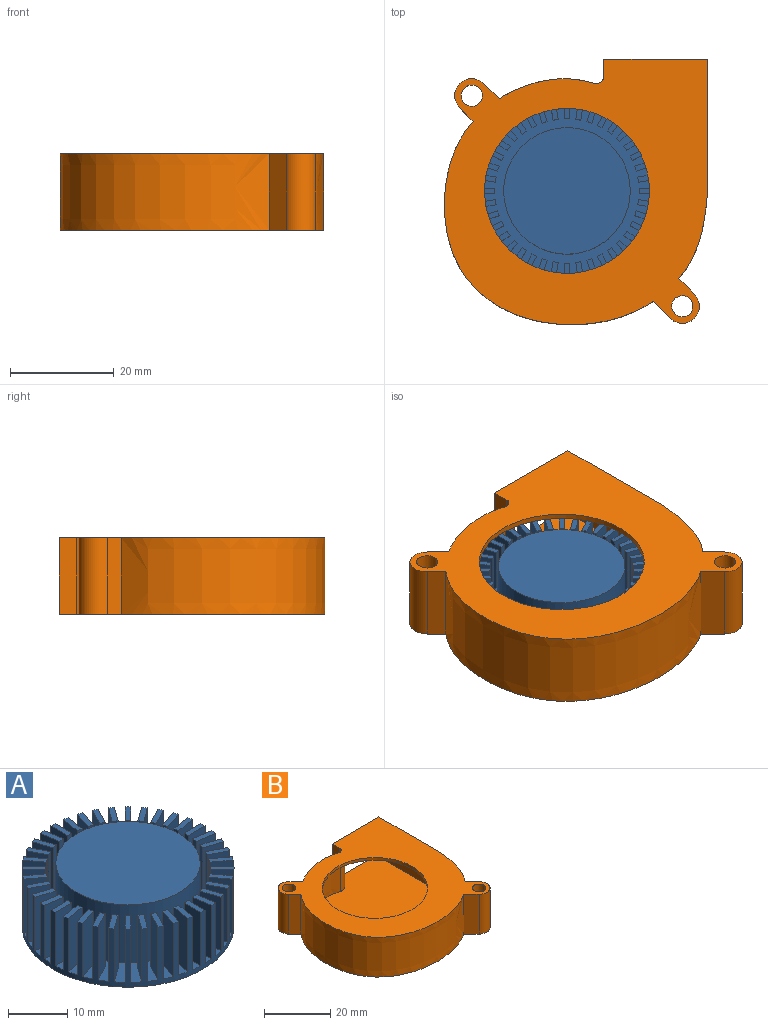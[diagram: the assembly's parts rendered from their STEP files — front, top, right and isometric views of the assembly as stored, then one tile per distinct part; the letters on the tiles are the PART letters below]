
ASSEMBLY  parts=2 mates=1
PART A: 165 faces, bbox 35.8x35.8x13 mm
  f0: plane 11x3.56mm, normal (-0.45,0.89,0), area 44mm2, adj f1,f3,f4,f6
  f1: cylinder r=17.91mm len=35.81mm, axis (0,0,-1), area 552.6mm2, adj f0,f2,f4,f5,f6,f7,f8,f10
  f2: plane 11x3.56mm, normal (0.45,-0.89,0), area 44mm2, adj f1,f3,f4,f6
  f3: plane 11x0.89mm, normal (0.89,0.45,0), area 11mm2, adj f0,f2,f4,f6
  f4: plane 4.02x2.71mm, normal (0,0,1), area 4mm2, adj f0,f1,f2,f3
  f5: plane 35.81x35.81mm, normal (0,0,-1), area 1007.4mm2, adj f1
  f6: plane 35.8x35.8mm, normal (0,0,1), area 379.6mm2, adj f0,f1,f2,f3,f7,f8,f9,f11
  f7: plane 11x3.8mm, normal (0.95,-0.31,0), area 44mm2, adj f1,f6,f9,f10
  f8: plane 11x3.8mm, normal (-0.95,0.31,0), area 44mm2, adj f1,f6,f9,f10
  f9: plane 11x0.95mm, normal (-0.31,-0.95,0), area 11mm2, adj f6,f7,f8,f10
  f10: plane 4.11x2.19mm, normal (0,0,1), area 4mm2, adj f1,f7,f8,f9
  f11: plane 11x3.95mm, normal (0.99,-0.16,0), area 44mm2, adj f1,f6,f13,f14
  f12: plane 11x3.95mm, normal (-0.99,0.16,0), area 44mm2, adj f1,f6,f13,f14
  f13: plane 11x0.99mm, normal (-0.16,-0.99,0), area 11mm2, adj f6,f11,f12,f14
  f14: plane 4.11x1.61mm, normal (0,0,1), area 4mm2, adj f1,f11,f12,f13
  f15: plane 11x3.8mm, normal (0.31,-0.95,0), area 44mm2, adj f1,f6,f17,f18
  f16: plane 11x3.8mm, normal (-0.31,0.95,0), area 44mm2, adj f1,f6,f17,f18
  f17: plane 11x0.95mm, normal (-0.95,-0.31,0), area 11mm2, adj f6,f15,f16,f18
  f18: plane 4.11x2.19mm, normal (0,0,1), area 4mm2, adj f1,f15,f16,f17
  f19: plane 11x3.56mm, normal (0.89,-0.45,0), area 44mm2, adj f1,f6,f21,f22
  f20: plane 11x3.56mm, normal (-0.89,0.45,0), area 44mm2, adj f1,f6,f21,f22
  f21: plane 11x0.89mm, normal (-0.45,-0.89,0), area 11mm2, adj f6,f19,f20,f22
  f22: plane 4.02x2.71mm, normal (0,0,1), area 4mm2, adj f1,f19,f20,f21
  f23: plane 11x3.95mm, normal (-0.99,-0.16,0), area 44mm2, adj f1,f6,f25,f26
  f24: plane 11x3.95mm, normal (0.99,0.16,0), area 44mm2, adj f1,f6,f25,f26
  f25: plane 11x0.99mm, normal (-0.16,0.99,0), area 11mm2, adj f6,f23,f24,f26
  f26: plane 4.11x1.61mm, normal (0,0,1), area 4mm2, adj f1,f23,f24,f25
  f27: plane 11x2.83mm, normal (-0.71,0.71,0), area 44mm2, adj f1,f6,f29,f30
  f28: plane 11x2.83mm, normal (0.71,-0.71,0), area 44mm2, adj f1,f6,f29,f30
  f29: plane 11x0.71mm, normal (0.71,0.71,0), area 11mm2, adj f6,f27,f28,f30
  f30: plane 3.54x3.54mm, normal (0,0,1), area 4mm2, adj f1,f27,f28,f29
  f31: plane 11x3.56mm, normal (-0.89,0.45,0), area 44mm2, adj f1,f6,f33,f34
  f32: plane 11x3.56mm, normal (0.89,-0.45,0), area 44mm2, adj f1,f6,f33,f34
  f33: plane 11x0.89mm, normal (0.45,0.89,0), area 11mm2, adj f6,f31,f32,f34
  f34: plane 4.02x2.71mm, normal (0,0,1), area 4mm2, adj f1,f31,f32,f33
  f35: plane 11x3.24mm, normal (-0.81,0.59,0), area 44mm2, adj f1,f6,f37,f38
  f36: plane 11x3.24mm, normal (0.81,-0.59,0), area 44mm2, adj f1,f6,f37,f38
  f37: plane 11x0.81mm, normal (0.59,0.81,0), area 11mm2, adj f6,f35,f36,f38
  f38: plane 3.82x3.16mm, normal (0,0,1), area 4mm2, adj f1,f35,f36,f37
  f39: plane 11x3.56mm, normal (0.45,-0.89,0), area 44mm2, adj f1,f6,f41,f42
  f40: plane 11x3.56mm, normal (-0.45,0.89,0), area 44mm2, adj f1,f6,f41,f42
  f41: plane 11x0.89mm, normal (-0.89,-0.45,0), area 11mm2, adj f6,f39,f40,f42
  f42: plane 4.02x2.71mm, normal (0,0,1), area 4mm2, adj f1,f39,f40,f41
  f43: plane 11x3.56mm, normal (-0.89,-0.45,0), area 44mm2, adj f1,f6,f45,f46
  f44: plane 11x3.56mm, normal (0.89,0.45,0), area 44mm2, adj f1,f6,f45,f46
  f45: plane 11x0.89mm, normal (-0.45,0.89,0), area 11mm2, adj f6,f43,f44,f46
  f46: plane 4.02x2.71mm, normal (0,0,1), area 4mm2, adj f1,f43,f44,f45
  f47: plane 11x3.24mm, normal (-0.59,0.81,0), area 44mm2, adj f1,f6,f49,f50
  f48: plane 11x3.24mm, normal (0.59,-0.81,0), area 44mm2, adj f1,f6,f49,f50
  f49: plane 11x0.81mm, normal (0.81,0.59,0), area 11mm2, adj f6,f47,f48,f50
  f50: plane 3.82x3.16mm, normal (0,0,1), area 4mm2, adj f1,f47,f48,f49
  f51: plane 11x3.8mm, normal (-0.31,0.95,0), area 44mm2, adj f1,f6,f53,f54
  f52: plane 11x3.8mm, normal (0.31,-0.95,0), area 44mm2, adj f1,f6,f53,f54
  f53: plane 11x0.95mm, normal (0.95,0.31,0), area 11mm2, adj f6,f51,f52,f54
  f54: plane 4.11x2.19mm, normal (0,0,1), area 4mm2, adj f1,f51,f52,f53
  f55: plane 11x3.95mm, normal (-0.16,0.99,0), area 44mm2, adj f1,f6,f57,f58
  f56: plane 11x3.95mm, normal (0.16,-0.99,0), area 44mm2, adj f1,f6,f57,f58
  f57: plane 11x0.99mm, normal (0.99,0.16,0), area 11mm2, adj f6,f55,f56,f58
  f58: plane 4.11x1.61mm, normal (0,0,1), area 4mm2, adj f1,f55,f56,f57
  f59: plane 11x3.8mm, normal (0.95,0.31,0), area 44mm2, adj f1,f6,f61,f62
  f60: plane 11x3.8mm, normal (-0.95,-0.31,0), area 44mm2, adj f1,f6,f61,f62
  f61: plane 11x0.95mm, normal (0.31,-0.95,0), area 11mm2, adj f6,f59,f60,f62
  f62: plane 4.11x2.19mm, normal (0,0,1), area 4mm2, adj f1,f59,f60,f61
  f63: plane 11x4mm, normal (0,1,0), area 44mm2, adj f1,f6,f65,f66
  f64: plane 11x4mm, normal (0,-1,0), area 44mm2, adj f1,f6,f65,f66
  f65: plane 11x1mm, normal (1,0,0), area 11mm2, adj f6,f63,f64,f66
  f66: plane 4.01x1mm, normal (0,0,1), area 4mm2, adj f1,f63,f64,f65
  f67: plane 11x3.8mm, normal (-0.95,-0.31,0), area 44mm2, adj f1,f6,f69,f70
  f68: plane 11x3.8mm, normal (0.95,0.31,0), area 44mm2, adj f1,f6,f69,f70
  f69: plane 11x0.95mm, normal (-0.31,0.95,0), area 11mm2, adj f6,f67,f68,f70
  f70: plane 4.11x2.19mm, normal (0,0,1), area 4mm2, adj f1,f67,f68,f69
  f71: plane 11x3.56mm, normal (0.89,0.45,0), area 44mm2, adj f1,f6,f73,f74
  f72: plane 11x3.56mm, normal (-0.89,-0.45,0), area 44mm2, adj f1,f6,f73,f74
  f73: plane 11x0.89mm, normal (0.45,-0.89,0), area 11mm2, adj f6,f71,f72,f74
  f74: plane 4.02x2.71mm, normal (0,0,1), area 4mm2, adj f1,f71,f72,f73
  f75: plane 11x2.83mm, normal (0.71,0.71,0), area 44mm2, adj f1,f6,f77,f78
  f76: plane 11x2.83mm, normal (-0.71,-0.71,0), area 44mm2, adj f1,f6,f77,f78
  f77: plane 11x0.71mm, normal (0.71,-0.71,0), area 11mm2, adj f6,f75,f76,f78
  f78: plane 3.54x3.54mm, normal (0,0,1), area 4mm2, adj f1,f75,f76,f77
  f79: cylinder r=12.2mm len=24.4mm, axis (0,0,-1), area 919.9mm2, adj f6,f80
  f80: plane 24.4x24.4mm, normal (0,0,1), area 467.6mm2, adj f79
  f81: plane 11x2.83mm, normal (0.71,-0.71,0), area 44mm2, adj f1,f6,f83,f84
  f82: plane 11x2.83mm, normal (-0.71,0.71,0), area 44mm2, adj f1,f6,f83,f84
  f83: plane 11x0.71mm, normal (-0.71,-0.71,0), area 11mm2, adj f6,f81,f82,f84
  f84: plane 3.54x3.54mm, normal (0,0,1), area 4mm2, adj f1,f81,f82,f83
  f85: plane 11x3.24mm, normal (0.81,-0.59,0), area 44mm2, adj f1,f6,f87,f88
  f86: plane 11x3.24mm, normal (-0.81,0.59,0), area 44mm2, adj f1,f6,f87,f88
  f87: plane 11x0.81mm, normal (-0.59,-0.81,0), area 11mm2, adj f6,f85,f86,f88
  f88: plane 3.82x3.16mm, normal (0,0,1), area 4mm2, adj f1,f85,f86,f87
  f89: plane 11x3.95mm, normal (0.16,-0.99,0), area 44mm2, adj f1,f6,f91,f92
  f90: plane 11x3.95mm, normal (-0.16,0.99,0), area 44mm2, adj f1,f6,f91,f92
  f91: plane 11x0.99mm, normal (-0.99,-0.16,0), area 11mm2, adj f6,f89,f90,f92
  f92: plane 4.11x1.61mm, normal (0,0,1), area 4mm2, adj f1,f89,f90,f91
  f93: plane 11x3.24mm, normal (0.59,-0.81,0), area 44mm2, adj f1,f6,f95,f96
  f94: plane 11x3.24mm, normal (-0.59,0.81,0), area 44mm2, adj f1,f6,f95,f96
  f95: plane 11x0.81mm, normal (-0.81,-0.59,0), area 11mm2, adj f6,f93,f94,f96
  f96: plane 3.82x3.16mm, normal (0,0,1), area 4mm2, adj f1,f93,f94,f95
  f97: plane 11x3.24mm, normal (0.59,0.81,0), area 44mm2, adj f1,f6,f99,f100
  f98: plane 11x3.24mm, normal (-0.59,-0.81,0), area 44mm2, adj f1,f6,f99,f100
  f99: plane 11x0.81mm, normal (0.81,-0.59,0), area 11mm2, adj f6,f97,f98,f100
  f100: plane 3.82x3.16mm, normal (0,0,1), area 4mm2, adj f1,f97,f98,f99
  f101: plane 11x3.24mm, normal (0.81,0.59,0), area 44mm2, adj f1,f6,f103,f104
  f102: plane 11x3.24mm, normal (-0.81,-0.59,0), area 44mm2, adj f1,f6,f103,f104
  f103: plane 11x0.81mm, normal (0.59,-0.81,0), area 11mm2, adj f6,f101,f102,f104
  f104: plane 3.82x3.16mm, normal (0,0,1), area 4mm2, adj f1,f101,f102,f103
  f105: plane 11x3.56mm, normal (-0.45,-0.89,0), area 44mm2, adj f1,f6,f107,f108
  f106: plane 11x3.56mm, normal (0.45,0.89,0), area 44mm2, adj f1,f6,f107,f108
  f107: plane 11x0.89mm, normal (-0.89,0.45,0), area 11mm2, adj f6,f105,f106,f108
  f108: plane 4.02x2.71mm, normal (0,0,1), area 4mm2, adj f1,f105,f106,f107
  f109: plane 11x4mm, normal (0,-1,0), area 44mm2, adj f1,f6,f111,f112
  f110: plane 11x4mm, normal (0,1,0), area 44mm2, adj f1,f6,f111,f112
  f111: plane 11x1mm, normal (-1,0,0), area 11mm2, adj f6,f109,f110,f112
  f112: plane 4.01x1mm, normal (0,0,1), area 4mm2, adj f1,f109,f110,f111
  f113: plane 11x3.95mm, normal (-0.16,-0.99,0), area 44mm2, adj f1,f6,f115,f116
  f114: plane 11x3.95mm, normal (0.16,0.99,0), area 44mm2, adj f1,f6,f115,f116
  f115: plane 11x0.99mm, normal (-0.99,0.16,0), area 11mm2, adj f6,f113,f114,f116
  f116: plane 4.11x1.61mm, normal (0,0,1), area 4mm2, adj f1,f113,f114,f115
  f117: plane 11x3.8mm, normal (-0.31,-0.95,0), area 44mm2, adj f1,f6,f119,f120
  f118: plane 11x3.8mm, normal (0.31,0.95,0), area 44mm2, adj f1,f6,f119,f120
  f119: plane 11x0.95mm, normal (-0.95,0.31,0), area 11mm2, adj f6,f117,f118,f120
  f120: plane 4.11x2.19mm, normal (0,0,1), area 4mm2, adj f1,f117,f118,f119
  f121: plane 11x3.24mm, normal (-0.81,-0.59,0), area 44mm2, adj f1,f6,f123,f124
  f122: plane 11x3.24mm, normal (0.81,0.59,0), area 44mm2, adj f1,f6,f123,f124
  f123: plane 11x0.81mm, normal (-0.59,0.81,0), area 11mm2, adj f6,f121,f122,f124
  f124: plane 3.82x3.16mm, normal (0,0,1), area 4mm2, adj f1,f121,f122,f123
  f125: plane 11x3.24mm, normal (-0.59,-0.81,0), area 44mm2, adj f1,f6,f127,f128
  f126: plane 11x3.24mm, normal (0.59,0.81,0), area 44mm2, adj f1,f6,f127,f128
  f127: plane 11x0.81mm, normal (-0.81,0.59,0), area 11mm2, adj f6,f125,f126,f128
  f128: plane 3.82x3.16mm, normal (0,0,1), area 4mm2, adj f1,f125,f126,f127
  f129: plane 11x2.83mm, normal (-0.71,-0.71,0), area 44mm2, adj f1,f6,f131,f132
  f130: plane 11x2.83mm, normal (0.71,0.71,0), area 44mm2, adj f1,f6,f131,f132
  f131: plane 11x0.71mm, normal (-0.71,0.71,0), area 11mm2, adj f6,f129,f130,f132
  f132: plane 3.54x3.54mm, normal (0,0,1), area 4mm2, adj f1,f129,f130,f131
  f133: plane 11x3.95mm, normal (0.99,0.16,0), area 44mm2, adj f1,f6,f135,f136
  f134: plane 11x3.95mm, normal (-0.99,-0.16,0), area 44mm2, adj f1,f6,f135,f136
  f135: plane 11x0.99mm, normal (0.16,-0.99,0), area 11mm2, adj f6,f133,f134,f136
  f136: plane 4.11x1.61mm, normal (0,0,1), area 4mm2, adj f1,f133,f134,f135
  f137: plane 11x3.8mm, normal (0.31,0.95,0), area 44mm2, adj f1,f6,f139,f140
  f138: plane 11x3.8mm, normal (-0.31,-0.95,0), area 44mm2, adj f1,f6,f139,f140
  f139: plane 11x0.95mm, normal (0.95,-0.31,0), area 11mm2, adj f6,f137,f138,f140
  f140: plane 4.11x2.19mm, normal (0,0,1), area 4mm2, adj f1,f137,f138,f139
  f141: plane 11x3.95mm, normal (0.16,0.99,0), area 44mm2, adj f1,f6,f143,f144
  f142: plane 11x3.95mm, normal (-0.16,-0.99,0), area 44mm2, adj f1,f6,f143,f144
  f143: plane 11x0.99mm, normal (0.99,-0.16,0), area 11mm2, adj f6,f141,f142,f144
  f144: plane 4.11x1.61mm, normal (0,0,1), area 4mm2, adj f1,f141,f142,f143
  f145: plane 11x3.95mm, normal (-0.99,0.16,0), area 44mm2, adj f1,f6,f147,f148
  f146: plane 11x3.95mm, normal (0.99,-0.16,0), area 44mm2, adj f1,f6,f147,f148
  f147: plane 11x0.99mm, normal (0.16,0.99,0), area 11mm2, adj f6,f145,f146,f148
  f148: plane 4.11x1.61mm, normal (0,0,1), area 4mm2, adj f1,f145,f146,f147
  f149: plane 11x3.8mm, normal (-0.95,0.31,0), area 44mm2, adj f1,f6,f151,f152
  f150: plane 11x3.8mm, normal (0.95,-0.31,0), area 44mm2, adj f1,f6,f151,f152
  f151: plane 11x0.95mm, normal (0.31,0.95,0), area 11mm2, adj f6,f149,f150,f152
  f152: plane 4.11x2.19mm, normal (0,0,1), area 4mm2, adj f1,f149,f150,f151
  f153: plane 11x3.56mm, normal (0.45,0.89,0), area 44mm2, adj f1,f6,f155,f156
  f154: plane 11x3.56mm, normal (-0.45,-0.89,0), area 44mm2, adj f1,f6,f155,f156
  f155: plane 11x0.89mm, normal (0.89,-0.45,0), area 11mm2, adj f6,f153,f154,f156
  f156: plane 4.02x2.71mm, normal (0,0,1), area 4mm2, adj f1,f153,f154,f155
  f157: plane 11x4mm, normal (-1,0,0), area 44mm2, adj f1,f6,f159,f160
  f158: plane 11x4mm, normal (1,0,0), area 44mm2, adj f1,f6,f159,f160
  f159: plane 11x1mm, normal (0,1,0), area 11mm2, adj f6,f157,f158,f160
  f160: plane 4.01x1mm, normal (0,0,1), area 4mm2, adj f1,f157,f158,f159
  f161: plane 11x1mm, normal (0,-1,0), area 11mm2, adj f6,f162,f163,f164
  f162: plane 11x4mm, normal (1,0,0), area 44mm2, adj f1,f6,f161,f164
  f163: plane 11x4mm, normal (-1,0,0), area 44mm2, adj f1,f6,f161,f164
  f164: plane 4.01x1mm, normal (0,0,1), area 4mm2, adj f1,f161,f162,f163
PART B: 24 faces, bbox 51.1x51.6x14.7 mm
  f0: extruded ~40.22x39.24mm, area 1058.7mm2, adj f8,f9,f18,f22
  f1: extruded ~18.42x14.7mm, area 283.1mm2, adj f6,f8,f9,f16
  f2: plane 20x14.7mm, normal (0,1,0), area 65.4mm2, adj f4,f5,f8,f9,f11,f12,f14,f15
  f3: extruded ~16.9x14.7mm, area 266.3mm2, adj f4,f8,f9,f21
  f4: plane 25.4x14.7mm, normal (1,0,0), area 373.4mm2, adj f2,f3,f8,f9
  f5: plane 14.7x3.36mm, normal (-1,0,0), area 49.4mm2, adj f2,f6,f8,f9
  f6: cylinder r=1.37mm len=14.7mm, axis (0,0,-1), area 37.5mm2, adj f1,f5,f8,f9
  f7: cylinder r=15.9mm len=31.8mm, axis (0,0,-1), area 99.9mm2, adj f8,f14
  f8: plane 51.6x51.1mm, normal (0,0,1), area 1386.1mm2, adj f0,f1,f2,f3,f4,f5,f6,f7
  f9: plane 51.6x51.1mm, normal (0,0,-1), area 2180.3mm2, adj f0,f1,f2,f3,f4,f5,f6,f16
  f10: extruded ~48.67x45.39mm, area 1495mm2, adj f11,f13,f14,f15
  f11: plane 25.37x12.7mm, normal (-1,0,0), area 322.2mm2, adj f2,f10,f14,f15
  f12: plane 12.7x3.36mm, normal (1,0,0), area 42.6mm2, adj f2,f13,f14,f15
  f13: cylinder r=2.37mm len=12.7mm, axis (0,0,-1), area 56.1mm2, adj f10,f12,f14,f15
  f14: plane 50.22x48.73mm, normal (0,0,-1), area 1172.9mm2, adj f2,f7,f10,f11,f12,f13
  f15: plane 50.22x48.73mm, normal (0,0,1), area 1967.1mm2, adj f2,f10,f11,f12,f13
  f16: plane 14.7x2.93mm, normal (0.71,0.71,0), area 60.9mm2, adj f1,f8,f9,f17
  f17: cylinder r=3.3mm len=14.7mm, axis (0,0,-1), area 152.4mm2, adj f8,f9,f16,f18
  f18: plane 14.7x2.57mm, normal (-0.71,-0.71,0), area 53.5mm2, adj f0,f8,f9,f17
  f19: cylinder r=2.05mm len=14.7mm, axis (0,0,-1), area 189.3mm2, adj f8,f9
  f20: cylinder r=3.3mm len=14.7mm, axis (0,0,-1), area 152.4mm2, adj f8,f9,f21,f22
  f21: plane 14.7x3mm, normal (0.71,0.71,0), area 62.4mm2, adj f3,f8,f9,f20
  f22: plane 14.7x3.28mm, normal (-0.71,-0.71,0), area 68.3mm2, adj f0,f8,f9,f20
  f23: cylinder r=2.05mm len=14.7mm, axis (0,0,-1), area 189.3mm2, adj f8,f9
PLACE A t=(0,0,-0.3)mm
PLACE B at identity
MATE revolute A.f1 <-> B.f7  axis (0,0,1) through (0,0,13.7)mm
